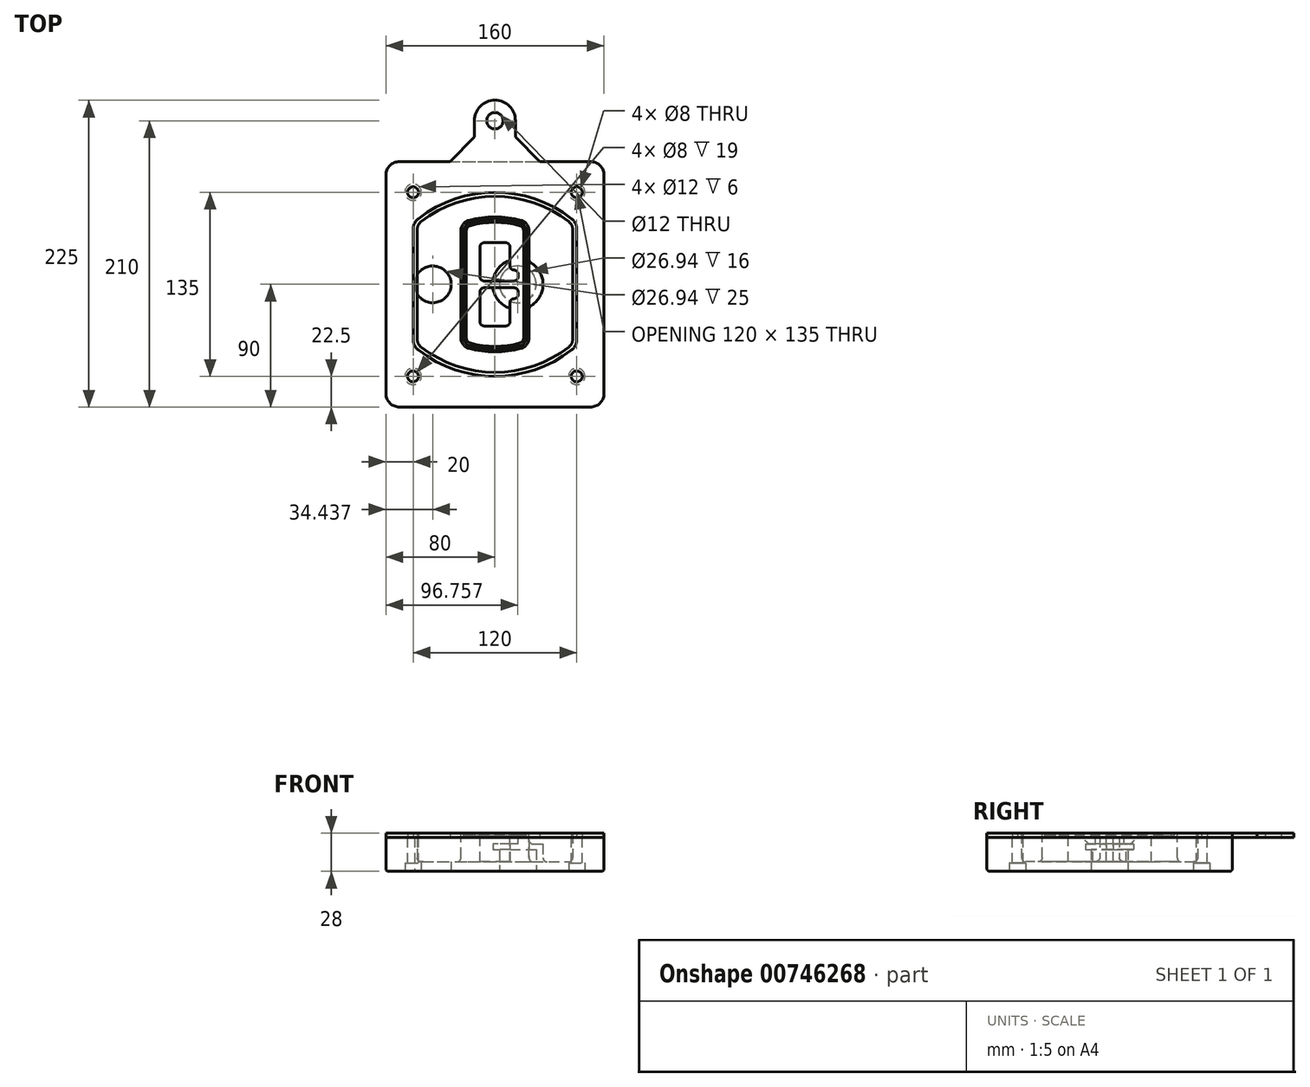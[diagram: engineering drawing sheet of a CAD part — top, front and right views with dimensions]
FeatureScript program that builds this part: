
annotation { "Feature Type Name" : "Feature", "Feature Type Description" : "" }
export const myFeature = defineFeature(function(context is Context, id is Id, definition is map)
    precondition{}
    {
        {
            var Q0;
            Q0=qCreatedBy(makeId("Top.planeOp"),FACE);
            var sketch = newSketch(context, id + "F0", { "sketchPlane" : qUnion([Q0])});
            skPoint(sketch, "E0.rect.middle", {"position": v(0, 0) * mm});
            skLineSegment(sketch, "E1.bottom", {"start": v(-70, -90) * mm, "end": v(70, -90) * mm});
            skLineSegment(sketch, "E1.top", {"start": v(-70, 90) * mm, "end": v(70, 90) * mm});
            skLineSegment(sketch, "E1.left", {"start": v(-80, -80) * mm, "end": v(-80, 80) * mm});
            skLineSegment(sketch, "E1.right", {"start": v(80, -80) * mm, "end": v(80, 80) * mm});
            skLineSegment(sketch, "E2", {"start": v(-80, 90) * mm, "end": v(80, -90) * mm, "construction": true});
            skLineSegment(sketch, "E3", {"start": v(80, 90) * mm, "end": v(-80, -90) * mm, "construction": true});
            skCircle(sketch, "E4", {"center": v(-60, 67.5) * mm, "radius": 4 * mm});
            skCircle(sketch, "E5", {"center": v(60, 67.5) * mm, "radius": 4 * mm});
            skCircle(sketch, "E6", {"center": v(60, -67.5) * mm, "radius": 4 * mm});
            skCircle(sketch, "E7", {"center": v(-60, -67.5) * mm, "radius": 4 * mm});
            skLineSegment(sketch, "E8", {"start": v(-60, 67.5) * mm, "end": v(60, 67.5) * mm, "construction": true});
            skLineSegment(sketch, "E9", {"start": v(60, 67.5) * mm, "end": v(60, -67.5) * mm, "construction": true});
            skLineSegment(sketch, "E10", {"start": v(60, -67.5) * mm, "end": v(-60, -67.5) * mm, "construction": true});
            skLineSegment(sketch, "E11", {"start": v(-60, -67.5) * mm, "end": v(-60, 67.5) * mm, "construction": true});
            skLineSegment(sketch, "E12", {"start": v(-60, 40.3) * mm, "end": v(-60, -40.3) * mm});
            skLineSegment(sketch, "E13", {"start": v(60, 40.3) * mm, "end": v(60, -40.3) * mm});
            skArc(sketch, "E14", {"start": v(56.15, 48.18) * mm, "mid": v(0, 67.5) * mm, "end": v(-56.15, 48.18) * mm});
            skArc(sketch, "E15", {"start": v(-56.15, -48.18) * mm, "mid": v(0, -67.5) * mm, "end": v(56.15, -48.18) * mm});
            skLineSegment(sketch, "E16", {"start": v(-60, 0) * mm, "end": v(60, 0) * mm, "construction": true});
            skPoint(sketch, "E17.visualSharp", {"position": v(-60, -45) * mm});
            skArc(sketch, "E17.filletArc", {"start": v(-60, -40.3) * mm, "mid": v(-58.99, -44.68) * mm, "end": v(-56.15, -48.18) * mm});
            skPoint(sketch, "E18.visualSharp", {"position": v(-60, 45) * mm});
            skArc(sketch, "E18.filletArc", {"start": v(-56.15, 48.18) * mm, "mid": v(-58.99, 44.68) * mm, "end": v(-60, 40.3) * mm});
            skPoint(sketch, "E19.visualSharp", {"position": v(60, 45) * mm});
            skArc(sketch, "E19.filletArc", {"start": v(60, 40.3) * mm, "mid": v(58.99, 44.68) * mm, "end": v(56.15, 48.18) * mm});
            skPoint(sketch, "E20.visualSharp", {"position": v(60, -45) * mm});
            skArc(sketch, "E20.filletArc", {"start": v(56.15, -48.18) * mm, "mid": v(58.99, -44.68) * mm, "end": v(60, -40.3) * mm});
            skPoint(sketch, "E21.visualSharp", {"position": v(-80, 90) * mm});
            skArc(sketch, "E21.filletArc", {"start": v(-70, 90) * mm, "mid": v(-77.07, 87.07) * mm, "end": v(-80, 80) * mm});
            skPoint(sketch, "E22.visualSharp", {"position": v(80, 90) * mm});
            skArc(sketch, "E22.filletArc", {"start": v(80, 80) * mm, "mid": v(77.07, 87.07) * mm, "end": v(70, 90) * mm});
            skPoint(sketch, "E23.visualSharp", {"position": v(80, -90) * mm});
            skArc(sketch, "E23.filletArc", {"start": v(70, -90) * mm, "mid": v(77.07, -87.07) * mm, "end": v(80, -80) * mm});
            skPoint(sketch, "E24.visualSharp", {"position": v(-80, -90) * mm});
            skArc(sketch, "E24.filletArc", {"start": v(-80, -80) * mm, "mid": v(-77.07, -87.07) * mm, "end": v(-70, -90) * mm});
            skArc(sketch, "E25.0", {"start": v(57, 40.3) * mm, "mid": v(56.3, 43.36) * mm, "end": v(54.3, 45.81) * mm});
            skLineSegment(sketch, "E25.1", {"start": v(57, 40.3) * mm, "end": v(57, -40.3) * mm});
            skArc(sketch, "E25.2", {"start": v(54.3, -45.81) * mm, "mid": v(56.3, -43.36) * mm, "end": v(57, -40.3) * mm});
            skArc(sketch, "E25.3", {"start": v(-54.3, -45.81) * mm, "mid": v(0, -64.5) * mm, "end": v(54.3, -45.81) * mm});
            skArc(sketch, "E25.4", {"start": v(-57, -40.3) * mm, "mid": v(-56.3, -43.36) * mm, "end": v(-54.3, -45.81) * mm});
            skArc(sketch, "E25.5", {"start": v(54.3, 45.81) * mm, "mid": v(0, 64.5) * mm, "end": v(-54.3, 45.81) * mm});
            skLineSegment(sketch, "E25.6", {"start": v(-57, 40.3) * mm, "end": v(-57, -40.3) * mm});
            skArc(sketch, "E25.7", {"start": v(-54.3, 45.81) * mm, "mid": v(-56.3, 43.36) * mm, "end": v(-57, 40.3) * mm});
            skArc(sketch, "E26.0", {"start": v(-58.62, 51.33) * mm, "mid": v(-62.58, 46.43) * mm, "end": v(-64, 40.3) * mm});
            skArc(sketch, "E26.1", {"start": v(58.62, 51.33) * mm, "mid": v(0, 71.5) * mm, "end": v(-58.62, 51.33) * mm});
            skArc(sketch, "E26.2", {"start": v(64, 40.3) * mm, "mid": v(62.58, 46.43) * mm, "end": v(58.62, 51.33) * mm});
            skLineSegment(sketch, "E26.3", {"start": v(64, 40.3) * mm, "end": v(64, -40.3) * mm});
            skArc(sketch, "E26.4", {"start": v(58.62, -51.33) * mm, "mid": v(62.58, -46.43) * mm, "end": v(64, -40.3) * mm});
            skLineSegment(sketch, "E26.5", {"start": v(-64, 40.3) * mm, "end": v(-64, -40.3) * mm});
            skArc(sketch, "E26.6", {"start": v(-58.62, -51.33) * mm, "mid": v(0, -71.5) * mm, "end": v(58.62, -51.33) * mm});
            skArc(sketch, "E26.7", {"start": v(-64, -40.3) * mm, "mid": v(-62.58, -46.43) * mm, "end": v(-58.62, -51.33) * mm});
            skSolve(sketch);
        }
        {
            var Q0;
            Q0=makeQuery(id+"F0.imprint","IMPRINT",FACE,{"disambiguationData":[TD([[makeQuery(id+"F0.imprint","IMPRINT",EDGE,{"derivedFrom":sQuery(id+"F0.wireOp",EDGE,"E1.bottom")}),1.0]])]});
            var Q1;
            Q1=makeQuery(id+"F0.imprint","IMPRINT",FACE,{"disambiguationData":[TD([[makeQuery(id+"F0.imprint","IMPRINT",EDGE,{"derivedFrom":sQuery(id+"F0.wireOp",EDGE,"E12")}),1.0]])]});
            var Q2;
            Q2=makeQuery(id+"F0.imprint","IMPRINT",FACE,{"disambiguationData":[TD([[makeQuery(id+"F0.imprint","IMPRINT",EDGE,{"derivedFrom":sQuery(id+"F0.wireOp",EDGE,"E25.0")}),1.0]])]});
            var Q3;
            Q3=makeQuery(id+"F0.imprint","IMPRINT",FACE,{"disambiguationData":[TD([[makeQuery(id+"F0.imprint","IMPRINT",EDGE,{"derivedFrom":sQuery(id+"F0.wireOp",EDGE,"E12")}),-1.0]])]});
            extrude(context, id + "F1", {"entities" : qUnion([Q0, Q1, Q2, Q3]), "oppositeDirection" : true, "depth" : 25 * mm});
        }
        {
            var Q0;
            Q0=makeQuery(id+"F0.imprint","IMPRINT",FACE,{"disambiguationData":[TD([[makeQuery(id+"F0.imprint","IMPRINT",EDGE,{"derivedFrom":sQuery(id+"F0.wireOp",EDGE,"E12")}),1.0]])]});
            extrude(context, id + "F2", {"entities" : qUnion([Q0]), "operationType" : NewBodyOperationType.ADD, "depth" : 3 * mm});
        }
        {
            var Q0;
            Q0=makeQuery(id+"F0.imprint","IMPRINT",FACE,{"disambiguationData":[TD([[makeQuery(id+"F0.imprint","IMPRINT",EDGE,{"derivedFrom":sQuery(id+"F0.wireOp",EDGE,"E25.0")}),1.0]])]});
            extrude(context, id + "F3", {"entities" : qUnion([Q0]), "operationType" : NewBodyOperationType.REMOVE, "oppositeDirection" : true, "depth" : 18 * mm});
        }
        {
            var Q0;
            Q0=makeQuery(id+"F2.opExtrude","CAP_FACE",FACE,{"disambiguationData":[OSD([sQuery(id+"F0.wireOp",EDGE,"E12"),sQuery(id+"F0.wireOp",EDGE,"E13"),sQuery(id+"F0.wireOp",EDGE,"E14"),sQuery(id+"F0.wireOp",EDGE,"E15"),sQuery(id+"F0.wireOp",EDGE,"E17.filletArc"),sQuery(id+"F0.wireOp",EDGE,"E18.filletArc"),sQuery(id+"F0.wireOp",EDGE,"E19.filletArc"),sQuery(id+"F0.wireOp",EDGE,"E20.filletArc"),sQuery(id+"F0.wireOp",EDGE,"E25.0"),sQuery(id+"F0.wireOp",EDGE,"E25.1"),sQuery(id+"F0.wireOp",EDGE,"E25.2"),sQuery(id+"F0.wireOp",EDGE,"E25.3"),sQuery(id+"F0.wireOp",EDGE,"E25.4"),sQuery(id+"F0.wireOp",EDGE,"E25.5"),sQuery(id+"F0.wireOp",EDGE,"E25.6"),sQuery(id+"F0.wireOp",EDGE,"E25.7")])],"isStart":false});
            var sketch = newSketch(context, id + "F4", { "sketchPlane" : qUnion([Q0])});
            skArc(sketch, "E27.0", {"start": v(-19.08, -46.97) * mm, "mid": v(0, -49.5) * mm, "end": v(19.08, -46.97) * mm});
            skArc(sketch, "E28.0", {"start": v(19.08, 46.97) * mm, "mid": v(0, 49.5) * mm, "end": v(-19.08, 46.97) * mm});
            skLineSegment(sketch, "E29", {"start": v(-25, 39.25) * mm, "end": v(-25, -39.25) * mm});
            skLineSegment(sketch, "E30", {"start": v(25, 39.25) * mm, "end": v(25, -39.25) * mm});
            skLineSegment(sketch, "E31", {"start": v(-25, 45.1) * mm, "end": v(25, 45.1) * mm, "construction": true});
            skLineSegment(sketch, "E32", {"start": v(-25, -45.1) * mm, "end": v(25, -45.1) * mm, "construction": true});
            skPoint(sketch, "E33.visualSharp", {"position": v(-25, 45.1) * mm});
            skArc(sketch, "E33.filletArc", {"start": v(-19.08, 46.97) * mm, "mid": v(-23.35, 44.11) * mm, "end": v(-25, 39.25) * mm});
            skPoint(sketch, "E34.visualSharp", {"position": v(25, 45.1) * mm});
            skArc(sketch, "E34.filletArc", {"start": v(25, 39.25) * mm, "mid": v(23.35, 44.11) * mm, "end": v(19.08, 46.97) * mm});
            skPoint(sketch, "E35.visualSharp", {"position": v(25, -45.1) * mm});
            skArc(sketch, "E35.filletArc", {"start": v(19.08, -46.97) * mm, "mid": v(23.35, -44.11) * mm, "end": v(25, -39.25) * mm});
            skPoint(sketch, "E36.visualSharp", {"position": v(-25, -45.1) * mm});
            skArc(sketch, "E36.filletArc", {"start": v(-25, -39.25) * mm, "mid": v(-23.35, -44.11) * mm, "end": v(-19.08, -46.97) * mm});
            skArc(sketch, "E37.0", {"start": v(54.3, 45.81) * mm, "mid": v(0, 64.5) * mm, "end": v(-54.3, 45.81) * mm});
            skArc(sketch, "E37.1", {"start": v(-54.3, 45.81) * mm, "mid": v(-56.3, 43.36) * mm, "end": v(-57, 40.3) * mm});
            skLineSegment(sketch, "E37.2", {"start": v(-57, 40.3) * mm, "end": v(-57, -40.3) * mm});
            skArc(sketch, "E37.3", {"start": v(-57, -40.3) * mm, "mid": v(-56.3, -43.36) * mm, "end": v(-54.3, -45.81) * mm});
            skArc(sketch, "E37.4", {"start": v(-54.3, -45.81) * mm, "mid": v(0, -64.5) * mm, "end": v(54.3, -45.81) * mm});
            skArc(sketch, "E37.5", {"start": v(54.3, -45.81) * mm, "mid": v(56.3, -43.36) * mm, "end": v(57, -40.3) * mm});
            skLineSegment(sketch, "E37.6", {"start": v(57, 40.3) * mm, "end": v(57, -40.3) * mm});
            skArc(sketch, "E37.7", {"start": v(57, 40.3) * mm, "mid": v(56.3, 43.36) * mm, "end": v(54.3, 45.81) * mm});
            skLineSegment(sketch, "E38.0", {"start": v(23, 39.25) * mm, "end": v(23, -39.25) * mm});
            skArc(sketch, "E38.1", {"start": v(18.56, -45.04) * mm, "mid": v(21.76, -42.9) * mm, "end": v(23, -39.25) * mm});
            skArc(sketch, "E38.2", {"start": v(-18.56, -45.04) * mm, "mid": v(0, -47.5) * mm, "end": v(18.56, -45.04) * mm});
            skArc(sketch, "E38.3", {"start": v(-23, -39.25) * mm, "mid": v(-21.76, -42.9) * mm, "end": v(-18.56, -45.04) * mm});
            skLineSegment(sketch, "E38.4", {"start": v(-23, 39.25) * mm, "end": v(-23, -39.25) * mm});
            skArc(sketch, "E38.5", {"start": v(23, 39.25) * mm, "mid": v(21.76, 42.9) * mm, "end": v(18.56, 45.04) * mm});
            skArc(sketch, "E38.6", {"start": v(-18.56, 45.04) * mm, "mid": v(-21.76, 42.9) * mm, "end": v(-23, 39.25) * mm});
            skArc(sketch, "E38.7", {"start": v(18.56, 45.04) * mm, "mid": v(0, 47.5) * mm, "end": v(-18.56, 45.04) * mm});
            skArc(sketch, "E39.0", {"start": v(21, 39.25) * mm, "mid": v(20.18, 41.68) * mm, "end": v(18.04, 43.1) * mm});
            skLineSegment(sketch, "E39.1", {"start": v(21, 39.25) * mm, "end": v(21, -39.25) * mm});
            skArc(sketch, "E39.2", {"start": v(18.04, -43.1) * mm, "mid": v(20.18, -41.68) * mm, "end": v(21, -39.25) * mm});
            skArc(sketch, "E39.3", {"start": v(-18.04, -43.1) * mm, "mid": v(0, -45.5) * mm, "end": v(18.04, -43.1) * mm});
            skArc(sketch, "E39.4", {"start": v(-21, -39.25) * mm, "mid": v(-20.18, -41.68) * mm, "end": v(-18.04, -43.1) * mm});
            skArc(sketch, "E39.5", {"start": v(18.04, 43.1) * mm, "mid": v(0, 45.5) * mm, "end": v(-18.04, 43.1) * mm});
            skLineSegment(sketch, "E39.6", {"start": v(-21, 39.25) * mm, "end": v(-21, -39.25) * mm});
            skArc(sketch, "E39.7", {"start": v(-18.04, 43.1) * mm, "mid": v(-20.18, 41.68) * mm, "end": v(-21, 39.25) * mm});
            skLineSegment(sketch, "E40", {"start": v(-25, 0) * mm, "end": v(25, 0) * mm, "construction": true});
            skLineSegment(sketch, "E41", {"start": v(-11, 5.5) * mm, "end": v(-11, 27.5) * mm});
            skLineSegment(sketch, "E42", {"start": v(-8, 30.5) * mm, "end": v(8, 30.5) * mm});
            skLineSegment(sketch, "E43", {"start": v(11, 27.5) * mm, "end": v(11, 13.5) * mm});
            skLineSegment(sketch, "E44", {"start": v(14, 10.5) * mm, "end": v(14, 10.5) * mm});
            skLineSegment(sketch, "E45", {"start": v(17, 7.5) * mm, "end": v(17, 5.5) * mm});
            skLineSegment(sketch, "E46", {"start": v(14, 2.5) * mm, "end": v(-8, 2.5) * mm});
            skPoint(sketch, "E47.visualSharp", {"position": v(-11, 30.5) * mm});
            skArc(sketch, "E47.filletArc", {"start": v(-8, 30.5) * mm, "mid": v(-10.12, 29.62) * mm, "end": v(-11, 27.5) * mm});
            skPoint(sketch, "E48.visualSharp", {"position": v(11, 30.5) * mm});
            skArc(sketch, "E48.filletArc", {"start": v(11, 27.5) * mm, "mid": v(10.12, 29.62) * mm, "end": v(8, 30.5) * mm});
            skPoint(sketch, "E49.visualSharp", {"position": v(11, 10.5) * mm});
            skArc(sketch, "E49.filletArc", {"start": v(11, 13.5) * mm, "mid": v(11.88, 11.38) * mm, "end": v(14, 10.5) * mm});
            skPoint(sketch, "E50.visualSharp", {"position": v(17, 10.5) * mm});
            skArc(sketch, "E50.filletArc", {"start": v(17, 7.5) * mm, "mid": v(16.12, 9.62) * mm, "end": v(14, 10.5) * mm});
            skPoint(sketch, "E51.visualSharp", {"position": v(17, 2.5) * mm});
            skArc(sketch, "E51.filletArc", {"start": v(14, 2.5) * mm, "mid": v(16.12, 3.38) * mm, "end": v(17, 5.5) * mm});
            skPoint(sketch, "E52.visualSharp", {"position": v(-11, 2.5) * mm});
            skArc(sketch, "E52.filletArc", {"start": v(-11, 5.5) * mm, "mid": v(-10.12, 3.38) * mm, "end": v(-8, 2.5) * mm});
            skLineSegment(sketch, "E53.0.MirrorCS", {"start": v(14, -2.5) * mm, "end": v(-8, -2.5) * mm});
            skArc(sketch, "E54.0.MirrorCS", {"start": v(-11, -5.5) * mm, "mid": v(-10.12, -3.38) * mm, "end": v(-8, -2.5) * mm});
            skLineSegment(sketch, "E55.0.MirrorCS", {"start": v(-11, -5.5) * mm, "end": v(-11, -27.5) * mm});
            skArc(sketch, "E56.0.MirrorCS", {"start": v(-8, -30.5) * mm, "mid": v(-10.12, -29.62) * mm, "end": v(-11, -27.5) * mm});
            skLineSegment(sketch, "E57.0.MirrorCS", {"start": v(-8, -30.5) * mm, "end": v(8, -30.5) * mm});
            skArc(sketch, "E58.0.MirrorCS", {"start": v(11, -27.5) * mm, "mid": v(10.12, -29.62) * mm, "end": v(8, -30.5) * mm});
            skLineSegment(sketch, "E59.0.MirrorCS", {"start": v(11, -27.5) * mm, "end": v(11, -13.5) * mm});
            skArc(sketch, "E60.0.MirrorCS", {"start": v(11, -13.5) * mm, "mid": v(11.88, -11.38) * mm, "end": v(14, -10.5) * mm});
            skArc(sketch, "E61.0.MirrorCS", {"start": v(17, -7.5) * mm, "mid": v(16.12, -9.62) * mm, "end": v(14, -10.5) * mm});
            skLineSegment(sketch, "E62.0.MirrorCS", {"start": v(17, -7.5) * mm, "end": v(17, -5.5) * mm});
            skArc(sketch, "E63.0.MirrorCS", {"start": v(14, -2.5) * mm, "mid": v(16.12, -3.38) * mm, "end": v(17, -5.5) * mm});
            skSolve(sketch);
        }
        {
            var Q0;
            Q0=makeQuery(id+"F4.imprint","IMPRINT",FACE,{"disambiguationData":[TD([[makeQuery(id+"F4.imprint","IMPRINT",EDGE,{"derivedFrom":sQuery(id+"F4.wireOp",EDGE,"E27.0")}),1.0]])]});
            var Q1;
            Q1=makeQuery(id+"F4.imprint","IMPRINT",FACE,{"disambiguationData":[TD([[makeQuery(id+"F4.imprint","IMPRINT",EDGE,{"derivedFrom":sQuery(id+"F4.wireOp",EDGE,"E38.0")}),-1.0]])]});
            var Q2;
            Q2=makeQuery(id+"F4.imprint","IMPRINT",FACE,{"disambiguationData":[TD([[makeQuery(id+"F4.imprint","IMPRINT",EDGE,{"derivedFrom":sQuery(id+"F4.wireOp",EDGE,"E39.0")}),1.0]])]});
            extrude(context, id + "F5", {"entities" : qUnion([Q0, Q1, Q2]), "operationType" : NewBodyOperationType.ADD, "endBound" : BoundingType.UP_TO_NEXT, "oppositeDirection" : true, "depth" : 25 * mm});
        }
        {
            var Q0;
            Q0=makeQuery(id+"F4.imprint","IMPRINT",FACE,{"disambiguationData":[TD([[makeQuery(id+"F4.imprint","IMPRINT",EDGE,{"derivedFrom":sQuery(id+"F4.wireOp",EDGE,"E38.0")}),-1.0]])]});
            extrude(context, id + "F6", {"entities" : qUnion([Q0]), "operationType" : NewBodyOperationType.REMOVE, "oppositeDirection" : true, "depth" : 2 * mm});
        }
        {
            var Q0;
            Q0=makeQuery(id+"F1.opExtrude","CAP_FACE",FACE,{"disambiguationData":[OSD([sQuery(id+"F0.wireOp",EDGE,"E1.bottom"),sQuery(id+"F0.wireOp",EDGE,"E1.top"),sQuery(id+"F0.wireOp",EDGE,"E1.left"),sQuery(id+"F0.wireOp",EDGE,"E1.right"),sQuery(id+"F0.wireOp",EDGE,"E4"),sQuery(id+"F0.wireOp",EDGE,"E5"),sQuery(id+"F0.wireOp",EDGE,"E6"),sQuery(id+"F0.wireOp",EDGE,"E7"),sQuery(id+"F0.wireOp",EDGE,"E21.filletArc"),sQuery(id+"F0.wireOp",EDGE,"E22.filletArc"),sQuery(id+"F0.wireOp",EDGE,"E23.filletArc"),sQuery(id+"F0.wireOp",EDGE,"E24.filletArc")])],"isStart":false});
            var sketch = newSketch(context, id + "F7", { "sketchPlane" : qUnion([Q0])});
            skCircle(sketch, "E64", {"center": v(16.76, 0) * mm, "radius": 13.47 * mm});
            skCircle(sketch, "E65", {"center": v(-45.56, 0) * mm, "radius": 13.47 * mm});
            skLineSegment(sketch, "E66", {"start": v(80, 0) * mm, "end": v(-80, 0) * mm});
            skCircle(sketch, "E67", {"center": v(16.76, 0) * mm, "radius": 18.47 * mm});
            skCircle(sketch, "E68", {"center": v(60, -67.5) * mm, "radius": 6 * mm});
            skCircle(sketch, "E69", {"center": v(-60, -67.5) * mm, "radius": 6 * mm});
            skCircle(sketch, "E70", {"center": v(-60, 67.5) * mm, "radius": 6 * mm});
            skCircle(sketch, "E71", {"center": v(60, 67.5) * mm, "radius": 6 * mm});
            skSolve(sketch);
        }
        {
            var Q0;
            {var subQ1=sQuery(id+"F7.wireOp",EDGE,"E66");var subQ4=sQuery(id+"F7.wireOp",EDGE,"E64");var subQ6=makeQuery(id+"F7.imprint","INTERSECT",VERTEX,{"disambiguationData":[OD(0.0)],"derivedFrom":[subQ4,subQ1]});Q0=makeQuery(id+"F7.imprint","IMPRINT",FACE,{"disambiguationData":[TD([[makeQuery(id+"F7.imprint","IMPRINT",EDGE,{"disambiguationData":[TD([[subQ6,-1.0]])],"derivedFrom":subQ4}),-1.0]])]});}
            var Q1;
            {var subQ0=sQuery(id+"F7.wireOp",EDGE,"E66");var subQ1=sQuery(id+"F7.wireOp",EDGE,"E64");var subQ3=makeQuery(id+"F7.imprint","INTERSECT",VERTEX,{"disambiguationData":[OD(0.0)],"derivedFrom":[subQ1,subQ0]});Q1=makeQuery(id+"F7.imprint","IMPRINT",FACE,{"disambiguationData":[TD([[makeQuery(id+"F7.imprint","IMPRINT",EDGE,{"disambiguationData":[TD([[subQ3,-1.0]])],"derivedFrom":subQ1}),1.0]])]});}
            var Q2;
            {var subQ0=sQuery(id+"F7.wireOp",EDGE,"E66");var subQ1=sQuery(id+"F7.wireOp",EDGE,"E64");var subQ3=makeQuery(id+"F7.imprint","INTERSECT",VERTEX,{"disambiguationData":[OD(0.0)],"derivedFrom":[subQ1,subQ0]});Q2=makeQuery(id+"F7.imprint","IMPRINT",FACE,{"disambiguationData":[TD([[makeQuery(id+"F7.imprint","IMPRINT",EDGE,{"disambiguationData":[TD([[subQ3,1.0]])],"derivedFrom":subQ1}),1.0]])]});}
            var Q3;
            {var subQ1=sQuery(id+"F7.wireOp",EDGE,"E66");var subQ4=sQuery(id+"F7.wireOp",EDGE,"E64");var subQ6=makeQuery(id+"F7.imprint","INTERSECT",VERTEX,{"disambiguationData":[OD(0.0)],"derivedFrom":[subQ4,subQ1]});Q3=makeQuery(id+"F7.imprint","IMPRINT",FACE,{"disambiguationData":[TD([[makeQuery(id+"F7.imprint","IMPRINT",EDGE,{"disambiguationData":[TD([[subQ6,1.0]])],"derivedFrom":subQ4}),-1.0]])]});}
            extrude(context, id + "F8", {"entities" : qUnion([Q0, Q1, Q2, Q3]), "operationType" : NewBodyOperationType.ADD, "oppositeDirection" : true, "depth" : 20 * mm});
        }
        {
            var Q0;
            {var subQ0=sQuery(id+"F7.wireOp",EDGE,"E66");var subQ1=sQuery(id+"F7.wireOp",EDGE,"E64");var subQ3=makeQuery(id+"F7.imprint","INTERSECT",VERTEX,{"disambiguationData":[OD(0.0)],"derivedFrom":[subQ1,subQ0]});Q0=makeQuery(id+"F7.imprint","IMPRINT",FACE,{"disambiguationData":[TD([[makeQuery(id+"F7.imprint","IMPRINT",EDGE,{"disambiguationData":[TD([[subQ3,-1.0]])],"derivedFrom":subQ1}),1.0]])]});}
            var Q1;
            {var subQ0=sQuery(id+"F7.wireOp",EDGE,"E66");var subQ1=sQuery(id+"F7.wireOp",EDGE,"E64");var subQ3=makeQuery(id+"F7.imprint","INTERSECT",VERTEX,{"disambiguationData":[OD(0.0)],"derivedFrom":[subQ1,subQ0]});Q1=makeQuery(id+"F7.imprint","IMPRINT",FACE,{"disambiguationData":[TD([[makeQuery(id+"F7.imprint","IMPRINT",EDGE,{"disambiguationData":[TD([[subQ3,1.0]])],"derivedFrom":subQ1}),1.0]])]});}
            extrude(context, id + "F9", {"entities" : qUnion([Q0, Q1]), "operationType" : NewBodyOperationType.REMOVE, "oppositeDirection" : true, "depth" : 16 * mm});
        }
        {
            var Q0;
            {var subQ0=sQuery(id+"F7.wireOp",EDGE,"E66");var subQ1=sQuery(id+"F7.wireOp",EDGE,"E65");var subQ3=makeQuery(id+"F7.imprint","INTERSECT",VERTEX,{"disambiguationData":[OD(0.0)],"derivedFrom":[subQ1,subQ0]});Q0=makeQuery(id+"F7.imprint","IMPRINT",FACE,{"disambiguationData":[TD([[makeQuery(id+"F7.imprint","IMPRINT",EDGE,{"disambiguationData":[TD([[subQ3,-1.0]])],"derivedFrom":subQ1}),1.0]])]});}
            var Q1;
            {var subQ0=sQuery(id+"F7.wireOp",EDGE,"E66");var subQ1=sQuery(id+"F7.wireOp",EDGE,"E65");var subQ3=makeQuery(id+"F7.imprint","INTERSECT",VERTEX,{"disambiguationData":[OD(0.0)],"derivedFrom":[subQ1,subQ0]});Q1=makeQuery(id+"F7.imprint","IMPRINT",FACE,{"disambiguationData":[TD([[makeQuery(id+"F7.imprint","IMPRINT",EDGE,{"disambiguationData":[TD([[subQ3,1.0]])],"derivedFrom":subQ1}),1.0]])]});}
            extrude(context, id + "F10", {"entities" : qUnion([Q0, Q1]), "operationType" : NewBodyOperationType.REMOVE, "oppositeDirection" : true, "depth" : 25 * mm});
        }
        {
            var Q0;
            Q0=makeQuery(id+"F7.imprint","IMPRINT",FACE,{"disambiguationData":[TD([[makeQuery(id+"F7.imprint","IMPRINT",EDGE,{"derivedFrom":sQuery(id+"F7.wireOp",EDGE,"E68")}),1.0]])]});
            var Q1;
            Q1=makeQuery(id+"F7.imprint","IMPRINT",FACE,{"disambiguationData":[TD([[makeQuery(id+"F7.imprint","IMPRINT",EDGE,{"derivedFrom":makeQuery(id+"F1.opExtrude","CAP_EDGE",EDGE,{"disambiguationData":[OSD([sQuery(id+"F0.wireOp",EDGE,"E5")])],"isStart":false})}),-1.0]])]});
            var Q2;
            Q2=makeQuery(id+"F7.imprint","IMPRINT",FACE,{"disambiguationData":[TD([[makeQuery(id+"F7.imprint","IMPRINT",EDGE,{"derivedFrom":sQuery(id+"F7.wireOp",EDGE,"E69")}),1.0]])]});
            var Q3;
            Q3=makeQuery(id+"F7.imprint","IMPRINT",FACE,{"disambiguationData":[TD([[makeQuery(id+"F7.imprint","IMPRINT",EDGE,{"derivedFrom":makeQuery(id+"F1.opExtrude","CAP_EDGE",EDGE,{"disambiguationData":[OSD([sQuery(id+"F0.wireOp",EDGE,"E4")])],"isStart":false})}),-1.0]])]});
            var Q4;
            Q4=makeQuery(id+"F7.imprint","IMPRINT",FACE,{"disambiguationData":[TD([[makeQuery(id+"F7.imprint","IMPRINT",EDGE,{"derivedFrom":sQuery(id+"F7.wireOp",EDGE,"E70")}),1.0]])]});
            var Q5;
            Q5=makeQuery(id+"F7.imprint","IMPRINT",FACE,{"disambiguationData":[TD([[makeQuery(id+"F7.imprint","IMPRINT",EDGE,{"derivedFrom":makeQuery(id+"F1.opExtrude","CAP_EDGE",EDGE,{"disambiguationData":[OSD([sQuery(id+"F0.wireOp",EDGE,"E7")])],"isStart":false})}),-1.0]])]});
            var Q6;
            Q6=makeQuery(id+"F7.imprint","IMPRINT",FACE,{"disambiguationData":[TD([[makeQuery(id+"F7.imprint","IMPRINT",EDGE,{"derivedFrom":sQuery(id+"F7.wireOp",EDGE,"E71")}),1.0]])]});
            var Q7;
            Q7=makeQuery(id+"F7.imprint","IMPRINT",FACE,{"disambiguationData":[TD([[makeQuery(id+"F7.imprint","IMPRINT",EDGE,{"derivedFrom":makeQuery(id+"F1.opExtrude","CAP_EDGE",EDGE,{"disambiguationData":[OSD([sQuery(id+"F0.wireOp",EDGE,"E6")])],"isStart":false})}),-1.0]])]});
            extrude(context, id + "F11", {"entities" : qUnion([Q0, Q1, Q2, Q3, Q4, Q5, Q6, Q7]), "operationType" : NewBodyOperationType.REMOVE, "oppositeDirection" : true, "depth" : 6 * mm});
        }
        {
            var Q0;
            Q0=makeQuery(id+"F9.boolean.opBoolean","COPY",FACE,{"derivedFrom":makeQuery(id+"F9.opExtrude","CAP_FACE",FACE,{"disambiguationData":[OSD([sQuery(id+"F7.wireOp",EDGE,"E64")])],"isStart":false})});
            var sketch = newSketch(context, id + "F12", { "sketchPlane" : qUnion([Q0])});
            skArc(sketch, "E72.0", {"start": v(11, 17.55) * mm, "mid": v(2.57, 11.82) * mm, "end": v(-1.54, 2.5) * mm});
            skArc(sketch, "E72.1", {"start": v(-1.54, -2.5) * mm, "mid": v(2.57, -11.82) * mm, "end": v(11, -17.55) * mm});
            skLineSegment(sketch, "E73", {"start": v(-1.54, -2.5) * mm, "end": v(14, -2.5) * mm});
            skLineSegment(sketch, "E74.0", {"start": v(14, 2.5) * mm, "end": v(-1.54, 2.5) * mm});
            skArc(sketch, "E74.1", {"start": v(14, 2.5) * mm, "mid": v(16.12, 3.38) * mm, "end": v(17, 5.5) * mm});
            skLineSegment(sketch, "E74.2", {"start": v(17, 7.5) * mm, "end": v(17, 5.5) * mm});
            skArc(sketch, "E74.3", {"start": v(17, 7.5) * mm, "mid": v(16.12, 9.62) * mm, "end": v(14, 10.5) * mm});
            skArc(sketch, "E74.4", {"start": v(11, 13.5) * mm, "mid": v(11.88, 11.38) * mm, "end": v(14, 10.5) * mm});
            skLineSegment(sketch, "E74.5", {"start": v(11, 17.55) * mm, "end": v(11, 13.5) * mm});
            skLineSegment(sketch, "E74.7", {"start": v(14, -2.5) * mm, "end": v(-1.54, -2.5) * mm});
            skArc(sketch, "E74.8", {"start": v(14, -2.5) * mm, "mid": v(16.12, -3.38) * mm, "end": v(17, -5.5) * mm});
            skLineSegment(sketch, "E74.9", {"start": v(17, -7.5) * mm, "end": v(17, -5.5) * mm});
            skArc(sketch, "E74.10", {"start": v(17, -7.5) * mm, "mid": v(16.12, -9.62) * mm, "end": v(14, -10.5) * mm});
            skArc(sketch, "E74.11", {"start": v(11, -13.5) * mm, "mid": v(11.88, -11.38) * mm, "end": v(14, -10.5) * mm});
            skLineSegment(sketch, "E74.12", {"start": v(11, -17.55) * mm, "end": v(11, -13.5) * mm});
            skPoint(sketch, "E75.orphan", {"position": v(11, -27.5) * mm});
            skPoint(sketch, "E76.orphan", {"position": v(-8, -2.5) * mm});
            skPoint(sketch, "E77.orphan", {"position": v(-8, 2.5) * mm});
            skPoint(sketch, "E78.orphan", {"position": v(11, 27.5) * mm});
            skSolve(sketch);
        }
        {
            var Q0;
            {var subQ7=sQuery(id+"F12.wireOp",EDGE,"E72.0");var subQ14=sQuery(id+"F12.wireOp",EDGE,"E72.1");var subQ16=sQuery(id+"F12.wireOp",EDGE,"E74.1");var subQ18=sQuery(id+"F12.wireOp",EDGE,"E74.8");Q0=qUnion([makeQuery(id+"F12.imprint","IMPRINT",FACE,{"disambiguationData":[TD([[makeQuery(id+"F12.imprint","IMPRINT",EDGE,{"derivedFrom":subQ7}),1.0]])]}),makeQuery(id+"F12.imprint","IMPRINT",FACE,{"disambiguationData":[TD([[makeQuery(id+"F12.imprint","IMPRINT",EDGE,{"derivedFrom":subQ14}),1.0]])]}),makeQuery(id+"F12.imprint","IMPRINT",FACE,{"disambiguationData":[TD([[makeQuery(id+"F12.imprint","IMPRINT",EDGE,{"derivedFrom":subQ16}),1.0]])]}),makeQuery(id+"F12.imprint","IMPRINT",FACE,{"disambiguationData":[TD([[makeQuery(id+"F12.imprint","IMPRINT",EDGE,{"derivedFrom":subQ18}),-1.0]])]})]);}
            var Q1;
            Q1=makeQuery(id+"F5.boolean.opBoolean","SPLIT",FACE,{"disambiguationData":[TD([makeQuery(id+"F5.opExtrude","SWEPT_FACE",FACE,{"disambiguationData":[OSD([sQuery(id+"F4.wireOp",EDGE,"E41")])]})])],"derivedFrom":makeQuery(id+"F3.boolean.opBoolean","COPY",FACE,{"derivedFrom":makeQuery(id+"F3.opExtrude","CAP_FACE",FACE,{"disambiguationData":[OSD([sQuery(id+"F0.wireOp",EDGE,"E25.0"),sQuery(id+"F0.wireOp",EDGE,"E25.1"),sQuery(id+"F0.wireOp",EDGE,"E25.2"),sQuery(id+"F0.wireOp",EDGE,"E25.3"),sQuery(id+"F0.wireOp",EDGE,"E25.4"),sQuery(id+"F0.wireOp",EDGE,"E25.5"),sQuery(id+"F0.wireOp",EDGE,"E25.6"),sQuery(id+"F0.wireOp",EDGE,"E25.7")])],"isStart":false})})});
            extrude(context, id + "F13", {"entities" : qUnion([Q0]), "operationType" : NewBodyOperationType.REMOVE, "endBound" : BoundingType.UP_TO_SURFACE, "endBoundEntityFace" : qUnion([Q1]), "depth" : 25 * mm});
        }
        {
            var Q0;
            Q0=makeQuery(id+"F3.boolean.opBoolean","COPY",EDGE,{"derivedFrom":makeQuery(id+"F3.opExtrude","CAP_EDGE",EDGE,{"disambiguationData":[OSD([sQuery(id+"F0.wireOp",EDGE,"E25.6")])],"isStart":false})});
            var Q1;
            Q1=makeQuery(id+"F8.boolean.opBoolean","INTERSECT",EDGE,{"derivedFrom":[makeQuery(id+"F5.opExtrude","SWEPT_FACE",FACE,{"disambiguationData":[OSD([sQuery(id+"F4.wireOp",EDGE,"E30")])]}),makeQuery(id+"F8.opExtrude","CAP_FACE",FACE,{"disambiguationData":[OSD([sQuery(id+"F7.wireOp",EDGE,"E67")])],"isStart":false})]});
            var Q2;
            Q2=makeQuery(id+"F8.boolean.opBoolean","INTERSECT",EDGE,{"disambiguationData":[OD(1.0)],"derivedFrom":[makeQuery(id+"F5.opExtrude","SWEPT_FACE",FACE,{"disambiguationData":[OSD([sQuery(id+"F4.wireOp",EDGE,"E30")])]}),makeQuery(id+"F8.opExtrude","SWEPT_FACE",FACE,{"disambiguationData":[OSD([sQuery(id+"F7.wireOp",EDGE,"E67")])]})]});
            var Q3;
            {var subQ0=sQuery(id+"F4.wireOp",EDGE,"E30");Q3=makeQuery(id+"F8.boolean.opBoolean","SPLIT",EDGE,{"disambiguationData":[TD([makeQuery(id+"F5.opExtrude","SWEPT_FACE",FACE,{"disambiguationData":[OSD([sQuery(id+"F4.wireOp",EDGE,"E35.filletArc")])]})])],"derivedFrom":makeQuery(id+"F5.opExtrude","CAP_EDGE",EDGE,{"disambiguationData":[OSD([subQ0])],"isStart":false})});}
            var Q4;
            {var subQ0=sQuery(id+"F0.wireOp",EDGE,"E25.7");var subQ1=sQuery(id+"F0.wireOp",EDGE,"E25.1");var subQ2=sQuery(id+"F0.wireOp",EDGE,"E25.6");var subQ3=sQuery(id+"F0.wireOp",EDGE,"E25.5");var subQ4=sQuery(id+"F0.wireOp",EDGE,"E25.4");var subQ5=sQuery(id+"F0.wireOp",EDGE,"E25.0");var subQ6=sQuery(id+"F0.wireOp",EDGE,"E25.2");var subQ7=sQuery(id+"F0.wireOp",EDGE,"E25.3");Q4=makeQuery(id+"F8.boolean.opBoolean","INTERSECT",EDGE,{"derivedFrom":[makeQuery(id+"F5.boolean.opBoolean","SPLIT",FACE,{"disambiguationData":[TD([makeQuery(id+"F2.opExtrude","SWEPT_FACE",FACE,{"disambiguationData":[OSD([subQ5])]})])],"derivedFrom":makeQuery(id+"F3.boolean.opBoolean","COPY",FACE,{"derivedFrom":makeQuery(id+"F3.opExtrude","CAP_FACE",FACE,{"disambiguationData":[OSD([subQ5,subQ1,subQ6,subQ7,subQ4,subQ3,subQ2,subQ0])],"isStart":false})})}),makeQuery(id+"F8.opExtrude","SWEPT_FACE",FACE,{"disambiguationData":[OSD([sQuery(id+"F7.wireOp",EDGE,"E67")])]})]});}
            var Q5;
            Q5=makeQuery(id+"F8.boolean.opBoolean","INTERSECT",EDGE,{"disambiguationData":[OD(0.0)],"derivedFrom":[makeQuery(id+"F5.opExtrude","SWEPT_FACE",FACE,{"disambiguationData":[OSD([sQuery(id+"F4.wireOp",EDGE,"E30")])]}),makeQuery(id+"F8.opExtrude","SWEPT_FACE",FACE,{"disambiguationData":[OSD([sQuery(id+"F7.wireOp",EDGE,"E67")])]})]});
            fillet(context, id + "F14", {"entities" : qUnion([Q0, Q1, Q2, Q3, Q4, Q5]), "radius" : 3 * mm, "tangentPropagation" : true, "allowEdgeOverflow" : false});
        }
        {
            var Q0;
            Q0=makeQuery(id+"F1.opExtrude","CAP_EDGE",EDGE,{"disambiguationData":[OSD([sQuery(id+"F0.wireOp",EDGE,"E1.bottom")])],"isStart":false});
            fillet(context, id + "F15", {"entities" : qUnion([Q0]), "radius" : 2 * mm, "tangentPropagation" : true, "allowEdgeOverflow" : false});
        }
        {
            var Q0;
            {var subQ0=sQuery(id+"F0.wireOp",EDGE,"E21.filletArc");var subQ1=sQuery(id+"F0.wireOp",EDGE,"E7");var subQ2=sQuery(id+"F0.wireOp",EDGE,"E6");var subQ3=sQuery(id+"F0.wireOp",EDGE,"E5");var subQ4=sQuery(id+"F0.wireOp",EDGE,"E4");var subQ5=sQuery(id+"F0.wireOp",EDGE,"E22.filletArc");var subQ6=sQuery(id+"F0.wireOp",EDGE,"E1.bottom");var subQ7=sQuery(id+"F0.wireOp",EDGE,"E1.right");var subQ8=sQuery(id+"F0.wireOp",EDGE,"E1.top");var subQ9=sQuery(id+"F0.wireOp",EDGE,"E1.left");var subQ10=sQuery(id+"F0.wireOp",EDGE,"E23.filletArc");var subQ11=sQuery(id+"F0.wireOp",EDGE,"E24.filletArc");Q0=makeQuery(id+"F2.boolean.opBoolean","SPLIT",FACE,{"disambiguationData":[TD([makeQuery(id+"F1.opExtrude","SWEPT_FACE",FACE,{"disambiguationData":[OSD([subQ6])]})])],"derivedFrom":makeQuery(id+"F1.opExtrude","CAP_FACE",FACE,{"disambiguationData":[OSD([subQ6,subQ8,subQ9,subQ7,subQ4,subQ3,subQ2,subQ1,subQ0,subQ5,subQ10,subQ11])],"isStart":true})});}
            var sketch = newSketch(context, id + "F16", { "sketchPlane" : qUnion([Q0])});
            skLineSegment(sketch, "E79", {"start": v(-15, 108) * mm, "end": v(-15, 120) * mm});
            skLineSegment(sketch, "E80", {"start": v(15, 108) * mm, "end": v(15, 120) * mm});
            skArc(sketch, "E81", {"start": v(15, 120) * mm, "mid": v(0, 135) * mm, "end": v(-15, 120) * mm});
            skCircle(sketch, "E82", {"center": v(0, 120) * mm, "radius": 6 * mm});
            skLineSegment(sketch, "E83", {"start": v(-74, 0) * mm, "end": v(75.2, 0) * mm, "construction": true});
            skArc(sketch, "E84.MirrorCS", {"start": v(15, -120) * mm, "mid": v(0, -135) * mm, "end": v(-15, -120) * mm});
            skLineSegment(sketch, "E85.MirrorCS", {"start": v(15, -108) * mm, "end": v(15, -120) * mm});
            skLineSegment(sketch, "E86.MirrorCS", {"start": v(-15, -108) * mm, "end": v(-15, -120) * mm});
            skCircle(sketch, "E87.MirrorC", {"center": v(0, -120) * mm, "radius": 6 * mm});
            skLineSegment(sketch, "E88", {"start": v(-15, 108) * mm, "end": v(-33, 90) * mm});
            skLineSegment(sketch, "E89", {"start": v(15, 108) * mm, "end": v(33, 90) * mm});
            skLineSegment(sketch, "E90", {"start": v(0, 90) * mm, "end": v(0, 120) * mm});
            skLineSegment(sketch, "E91.MirrorCS", {"start": v(-15, -108) * mm, "end": v(-33, -90) * mm});
            skLineSegment(sketch, "E92.MirrorCS", {"start": v(15, -108) * mm, "end": v(33, -90) * mm});
            skLineSegment(sketch, "E93.MirrorCS", {"start": v(0, -90) * mm, "end": v(0, -120) * mm});
            skSolve(sketch);
        }
        {
            var Q0;
            Q0=makeQuery(id+"F16.imprint","IMPRINT",FACE,{"disambiguationData":[TD([[makeQuery(id+"F16.imprint","IMPRINT",EDGE,{"derivedFrom":makeQuery(id+"F1.opExtrude","CAP_EDGE",EDGE,{"disambiguationData":[OSD([sQuery(id+"F0.wireOp",EDGE,"E1.left")])],"isStart":true})}),-1.0]])]});
            var Q1;
            Q1=makeQuery(id+"F16.imprint","IMPRINT",FACE,{"disambiguationData":[TD([[makeQuery(id+"F16.imprint","IMPRINT",EDGE,{"derivedFrom":sQuery(id+"F16.wireOp",EDGE,"E79")}),-1.0]])]});
            var Q2;
            Q2=makeQuery(id+"F16.imprint","IMPRINT",FACE,{"disambiguationData":[TD([[makeQuery(id+"F16.imprint","IMPRINT",EDGE,{"derivedFrom":sQuery(id+"F16.wireOp",EDGE,"E84.MirrorCS")}),-1.0]])]});
            var Q3;
            Q3=makeQuery(id+"F2.opExtrude","CAP_FACE",FACE,{"disambiguationData":[OSD([sQuery(id+"F0.wireOp",EDGE,"E12"),sQuery(id+"F0.wireOp",EDGE,"E13"),sQuery(id+"F0.wireOp",EDGE,"E14"),sQuery(id+"F0.wireOp",EDGE,"E15"),sQuery(id+"F0.wireOp",EDGE,"E17.filletArc"),sQuery(id+"F0.wireOp",EDGE,"E18.filletArc"),sQuery(id+"F0.wireOp",EDGE,"E19.filletArc"),sQuery(id+"F0.wireOp",EDGE,"E20.filletArc"),sQuery(id+"F0.wireOp",EDGE,"E25.0"),sQuery(id+"F0.wireOp",EDGE,"E25.1"),sQuery(id+"F0.wireOp",EDGE,"E25.2"),sQuery(id+"F0.wireOp",EDGE,"E25.3"),sQuery(id+"F0.wireOp",EDGE,"E25.4"),sQuery(id+"F0.wireOp",EDGE,"E25.5"),sQuery(id+"F0.wireOp",EDGE,"E25.6"),sQuery(id+"F0.wireOp",EDGE,"E25.7")])],"isStart":false});
            extrude(context, id + "F17", {"entities" : qUnion([Q0, Q1, Q2]), "endBound" : BoundingType.UP_TO_SURFACE, "depth" : 25 * mm, "endBoundEntityFace" : qUnion([Q3]), "offsetDistance" : 25 * mm});
        }
    });
